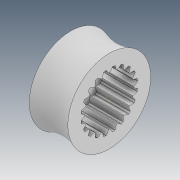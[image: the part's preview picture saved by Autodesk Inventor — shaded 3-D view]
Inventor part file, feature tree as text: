
AUTODESK INVENTOR PART (.ipt)
format: ipt  version: 2021 (Build 250183000, 183)  size: 319,488 bytes
history: native  units: in
note: dims shown in document units (in); Inventor stores cm internally (conversion verified against a paired STEP export)
features: other x2, sketch x2, extrude x1
ambient origin geometry x8: Origin, YZ Plane, XZ Plane, XY Plane, X Axis, Y Axis, Z Axis, Center Point
bodies: Body1 (feature_tree)
feature tree (5):
  other  "Sólido1"
  other  "Revolução1"
  extrude  "Extrusão5"  Depth=0.1693in
  sketch  "Esboço12"  dims[d0=0.1575in d1=0.1693in]
  sketch  "Esboço13"  dims[d2=90.0deg d58=0.2008in d59=0.2323in d60=0.0024in d61=0.0024in d62=0.002in d63=0.002in d64=7.874in d66=360.0deg d68=0.1378in d69=0.0in d70=0.2165in]
